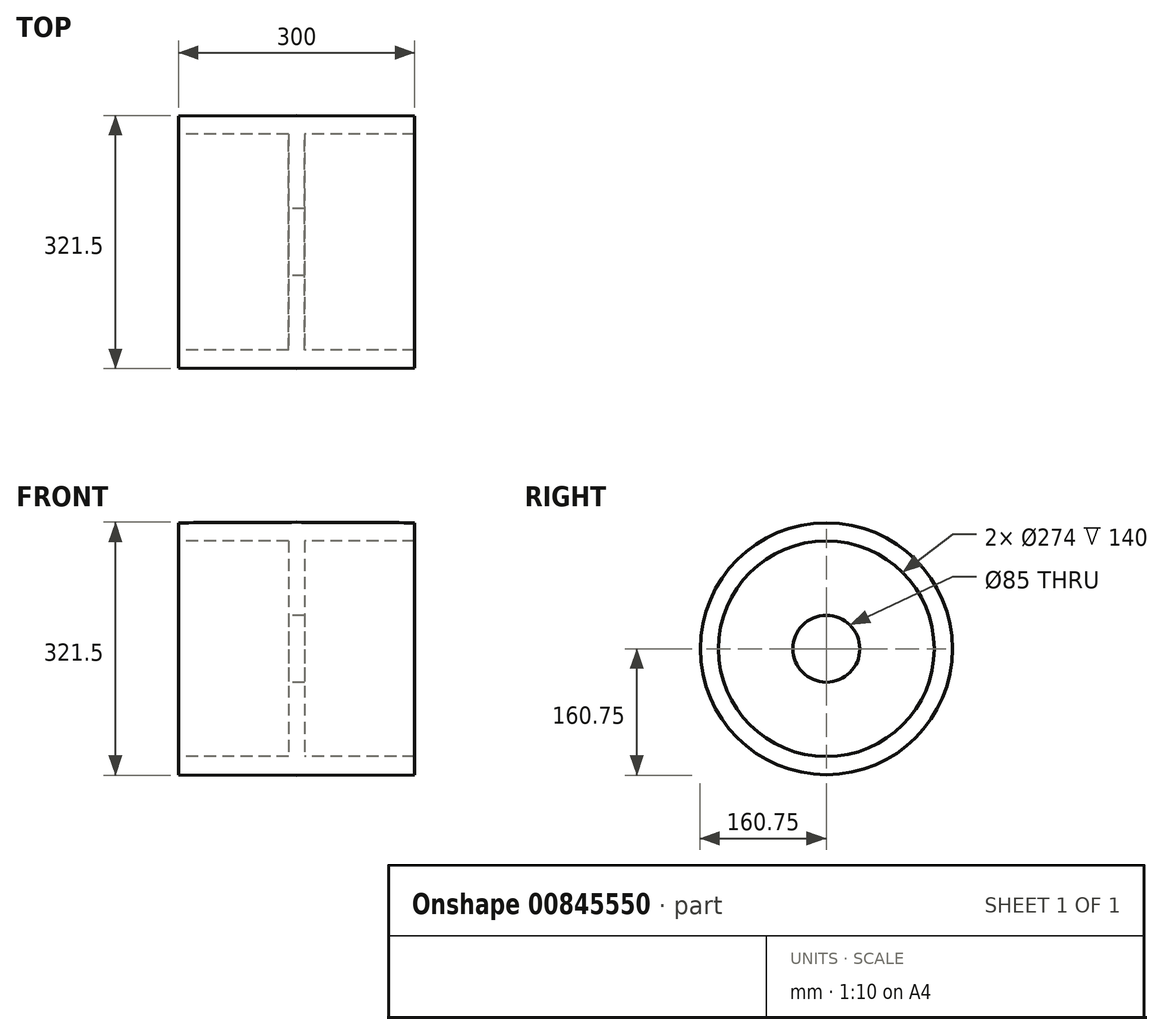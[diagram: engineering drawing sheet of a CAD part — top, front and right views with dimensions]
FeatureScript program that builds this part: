
annotation { "Feature Type Name" : "Feature", "Feature Type Description" : "" }
export const myFeature = defineFeature(function(context is Context, id is Id, definition is map)
    precondition{}
    {
        {
            var Q0;
            Q0=qCreatedBy(makeId("Front.planeOp"),FACE);
            var sketch = newSketch(context, id + "F0", { "sketchPlane" : qUnion([Q0])});
            skLineSegment(sketch, "E0", {"start": v(-150, 137) * mm, "end": v(150, 137) * mm});
            skLineSegment(sketch, "E1", {"start": v(-150, 137) * mm, "end": v(-150, 160) * mm});
            skLineSegment(sketch, "E2", {"start": v(150, 137) * mm, "end": v(150, 160) * mm});
            skLineSegment(sketch, "E3", {"start": v(-40.63, 213.06) * mm, "end": v(59.37, 213.06) * mm});
            skLineSegment(sketch, "E4", {"start": v(59.37, 213.06) * mm, "end": v(59.37, 233.06) * mm});
            skLineSegment(sketch, "E5", {"start": v(-40.63, 213.06) * mm, "end": v(-40.63, 233.56) * mm});
            skLineSegment(sketch, "E6", {"start": v(-40.63, 233.56) * mm, "end": v(59.37, 233.06) * mm});
            skLineSegment(sketch, "E7", {"start": v(-10, 137) * mm, "end": v(-10, 42.5) * mm});
            skLineSegment(sketch, "E8", {"start": v(10, 137) * mm, "end": v(10, 42.5) * mm});
            skLineSegment(sketch, "E9", {"start": v(-150, 0) * mm, "end": v(150, 0) * mm});
            skLineSegment(sketch, "E10", {"start": v(-10, 42.5) * mm, "end": v(10, 42.5) * mm});
            skPoint(sketch, "E11", {"position": v(0, 160.75) * mm});
            skPoint(sketch, "E11.positionSnap0", {"position": v(0, 137) * mm});
            skLineSegment(sketch, "E12", {"start": v(-150, 160) * mm, "end": v(0, 160.75) * mm});
            skLineSegment(sketch, "E13", {"start": v(150, 160) * mm, "end": v(0, 160.75) * mm});
            skSolve(sketch);
        }
        {
            var Q0;
            Q0=makeQuery(id+"F0.imprint","IMPRINT",FACE,{"disambiguationData":[TD([[makeQuery(id+"F0.imprint","IMPRINT",EDGE,{"derivedFrom":sQuery(id+"F0.wireOp",EDGE,"E0")}),1.0]])]});
            var Q1;
            {var subQ0=sQuery(id+"F0.wireOp",EDGE,"E7");Q1=makeQuery(id+"F0.imprint","IMPRINT",FACE,{"disambiguationData":[TD([[makeQuery(id+"F0.imprint","IMPRINT",EDGE,{"derivedFrom":subQ0}),1.0]])]});}
            var Q2;
            Q2=sQuery(id+"F0.wireOp",EDGE,"E9");
            revolve(context, id + "F1", {"surfaceOperationType" : NewSurfaceOperationType.NEW, "entities" : qUnion([Q0, Q1]), "axis" : qUnion([Q2]), "revolveType" : RevolveType.FULL});
        }
    });
